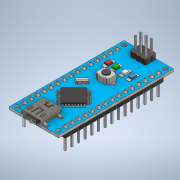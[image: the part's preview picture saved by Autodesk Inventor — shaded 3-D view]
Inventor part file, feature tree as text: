
AUTODESK INVENTOR PART (.ipt)
format: ipt  version: 2021 (Build 250183000, 183)  size: 2,560,000 bytes
history: native  units: mm
features: extrude x33, sketch x32, projected_geometry x27, chamfer x26, fillet x25, mirror x4, plane x3, pattern_circular x1
ambient origin geometry x8: Origin, YZ Plane, XZ Plane, XY Plane, X Axis, Y Axis, Z Axis, Center Point
bodies: Solid1 (feature_tree)
feature tree (151):
  extrude  "Extrusion1"  Depth=18.54199mm
  sketch  "Sketch2"  dims[d2=1.523999mm d3=1.523999mm]
  extrude  "Extrusion2"  Depth=1.523999mm
  extrude  "Extrusion3"  Depth=1.523999mm
  chamfer  "Chamfer1"  Distance=1.0mm
  chamfer  "Chamfer2"  Distance=1.0mm
  chamfer  "Chamfer3"  Distance=0.3mm
  chamfer  "Chamfer4"  Distance=0.7mm Angle=45.0deg
  chamfer  "Chamfer5"  Distance=0.7mm Angle=45.0deg
  chamfer  "Chamfer6"  Distance=0.7mm Angle=45.0deg
  chamfer  "Chamfer7"  Distance=0.7mm Angle=45.0deg
  chamfer  "Chamfer8"  Distance=0.7mm Angle=45.0deg
  chamfer  "Chamfer9"  Distance=0.7mm Angle=45.0deg
  chamfer  "Chamfer10"  Distance=0.7mm Angle=45.0deg
  chamfer  "Chamfer11"  Distance=0.7mm Angle=45.0deg
  chamfer  "Chamfer12"  Distance=0.7mm Angle=45.0deg
  chamfer  "Chamfer13"  Distance=0.7mm Angle=45.0deg
  chamfer  "Chamfer14"  Distance=0.7mm Angle=45.0deg
  chamfer  "Chamfer15"  Distance=0.7mm Angle=45.0deg
  fillet  "Fillet1"  Radius=0.2mm
  sketch  "Sketch6"  dims[d6=1.523999mm]
  plane  "Work Plane1"
  mirror  "Mirror1"
  extrude  "Extrusion5"  Depth=14.0mm TaperAngle=0.0deg
  extrude  "Extrusion6"  Depth=6.0mm TaperAngle=0.0deg
  extrude  "Extrusion7"  Depth=5.0mm
  extrude  "Extrusion8"  Depth=0.3mm
  fillet  "Fillet2"  Radius=0.2mm
  fillet  "Fillet3"  Radius=2.0mm
  fillet  "Fillet4"  Radius=0.5mm
  fillet  "Fillet5"  Radius=0.3mm
  extrude  "Extrusion9"  Depth=0.3mm
  extrude  "Extrusion10"  Depth=1.0mm TaperAngle=0.0deg
  extrude  "Extrusion11"  Depth=0.2mm
  fillet  "Fillet6"  Radius=0.2mm
  fillet  "Fillet7"  Radius=0.1mm
  plane  "Work Plane2"
  mirror  "Mirror2"
  extrude  "Extrusion12"  Depth=1.0mm
  extrude  "Extrusion13"  Depth=8.0mm TaperAngle=0.0deg
  extrude  "Extrusion14"  Depth=0.2mm
  extrude  "Extrusion15"  Depth=0.3mm
  extrude  "Extrusion16"  Depth=0.3mm
  fillet  "Fillet8"  Radius=0.3mm
  fillet  "Fillet9"  Radius=0.5mm
  sketch  "Sketch19"  dims[d115=5.0mm d116=0.0mm d117=0.07mm]
  extrude  "Extrusion17"  Depth=1.0mm TaperAngle=360.0deg
  extrude  "Extrusion18"  Depth=0.2mm
  pattern_circular  "Circular Pattern1"  Angle=45.0deg  [1 undecoded]
  extrude  "Extrusion19"  Depth=0.5mm
  fillet  "Fillet10"  Radius=0.4mm
  fillet  "Fillet11"  Radius=0.5mm
  extrude  "Extrusion20"  Depth=0.4mm
  extrude  "Extrusion21"  Depth=0.7mm TaperAngle=0.0deg
  chamfer  "Chamfer16"  Distance=5.0mm
  fillet  "Fillet12"  Radius=3.5mm
  extrude  "Extrusion22"  Depth=0.3mm
  extrude  "Extrusion23"  Depth=2.0mm TaperAngle=0.0deg
  extrude  "Extrusion24"  Depth=2.5mm
  sketch  "Sketch28"  dims[d174=0.5mm d175=0.0mm d176=0.2mm]
  extrude  "Extrusion25"  Depth=0.2mm TaperAngle=0.0deg
  extrude  "Extrusion26"  Depth=0.7mm TaperAngle=0.0deg
  extrude  "Extrusion27"  Depth=0.2mm TaperAngle=0.0deg
  extrude  "Extrusion28"  Depth=0.2mm
  mirror  "Mirror3"
  fillet  "Fillet13"  Radius=4.0mm
  fillet  "Fillet14"  [1 undecoded]
  fillet  "Fillet15"  Radius=1.1mm
  fillet  "Fillet16"  Radius=1.1mm
  extrude  "Extrusion29"  Depth=0.5mm
  fillet  "Fillet17"  Radius=0.2mm
  fillet  "Fillet18"  Radius=0.2mm
  fillet  "Fillet19"  Radius=0.2mm
  fillet  "Fillet20"  Radius=0.4mm
  fillet  "Fillet21"  Radius=0.2mm
  fillet  "Fillet22"  Radius=0.2mm
  fillet  "Fillet23"  Radius=0.2mm
  fillet  "Fillet24"  Radius=0.2mm
  extrude  "Extrusion30"  Depth=0.2mm
  extrude  "Extrusion31"  Depth=0.2mm
  plane  "Work Plane3"
  extrude  "Extrusion32"  Depth=0.2mm
  extrude  "Extrusion33"  Depth=0.2mm
  chamfer  "Chamfer17"  Distance=3.0mm
  chamfer  "Chamfer18"  Distance=1.25mm
  chamfer  "Chamfer19"  Distance=1.25mm
  chamfer  "Chamfer20"  Distance=0.4mm
  mirror  "Mirror4"
  extrude  "Extrusion34"  Depth=0.4mm
  chamfer  "Chamfer21"  Distance=0.4mm
  chamfer  "Chamfer22"  Distance=0.4mm
  chamfer  "Chamfer23"  Distance=0.4mm
  chamfer  "Chamfer24"  Distance=0.4mm
  chamfer  "Chamfer25"  Distance=0.4mm
  chamfer  "Chamfer26"  Distance=0.4mm
  fillet  "Fillet25"  Radius=0.4mm
  sketch  "Sketch38"  dims[d217=5.0mm d218=0.0mm d219=0.2mm d220=0.5725mm d221=45.0deg d222=0.5mm d235=0.4mm d236=0.0mm d237=0.5mm d238=0.0mm d239=0.4mm d240=0.7mm d241=0.0mm d243=5.0mm d244=3.5mm d245=0.3mm d256=2.0mm d257=0.0mm d259=2.5mm d260=0.6mm d261=0.0mm d262=0.7mm d263=0.0mm d266=0.58mm d267=0.0mm d268=8.597851mm d269=4.0mm d270=0.0mm d273=1.1mm d274=1.1mm d275=0.5mm d276=0.2mm d277=0.2mm d278=0.2mm d279=0.4mm d280=0.0mm d281=0.2mm d282=0.2mm d283=0.2mm d284=0.2mm d285=0.2mm d286=0.2mm d287=0.2mm d288=0.2mm d289=3.0mm d290=0.0mm d297=1.25mm d298=1.25mm d311=0.4mm d312=0.4mm d313=0.4mm d314=0.4mm d315=0.4mm d316=0.4mm d317=0.4mm d318=0.4mm d319=0.4mm d320=0.4mm d321=0.4mm d322=0.4mm d323=0.4mm d324=0.4mm d325=0.4mm d326=0.4mm d327=0.4mm d328=0.4mm d330=2.5mm d331=0.4mm d332=0.4mm d333=1.9mm d334=0.0mm d335=0.0mm d336=0.1mm d337=0.0mm d338=5.0mm d339=0.0mm d340=0.2mm d341=0.5725mm d342=45.0deg d343=0.2mm d344=0.5725mm d345=45.0deg d346=0.2mm d347=0.5725mm d348=45.0deg d349=0.2mm d350=0.5725mm d351=45.0deg d358=1.2mm d359=0.0mm d360=0.6mm d361=1.2mm d362=45.0deg d363=0.6mm d364=1.2mm d365=45.0deg d366=0.6mm d367=1.2mm d368=45.0deg d369=0.6mm d370=1.2mm d371=45.0deg d372=0.6mm d373=1.2mm d374=45.0deg d375=0.6mm d376=1.2mm d377=45.0deg d378=0.2mm]
  sketch  "Sketch1"  dims[d0=43.17998mm d1=18.54199mm]
  sketch  "Sketch3"  dims[d4=1.523999mm d5=1.523999mm]
  projected_geometry  "Projected Loop1"
  projected_geometry  "Projected Loop2"
  projected_geometry  "Projected Loop3"
  projected_geometry  "Projected Loop4"
  projected_geometry  "Projected Loop5"
  projected_geometry  "Projected Loop6"
  projected_geometry  "Projected Loop7"
  projected_geometry  "Projected Loop8"
  projected_geometry  "Projected Loop9"
  projected_geometry  "Projected Loop10"
  projected_geometry  "Projected Loop11"
  projected_geometry  "Projected Loop12"
  projected_geometry  "Projected Loop13"
  sketch  "Sketch7"  dims[d7=0.0mm]
  projected_geometry  "Projected Loop25"
  sketch  "Sketch8"  dims[d8=1.523999mm]
  projected_geometry  "Projected Loop26"
  sketch  "Sketch9"  dims[d9=0.0mm]
  projected_geometry  "Projected Loop27"
  sketch  "Sketch10"  dims[d10=1.777999mm]
  projected_geometry  "Projected Loop28"
  sketch  "Sketch11"  dims[d11=1.777999mm]
  projected_geometry  "Projected Loop29"
  sketch  "Sketch12"  dims[d12=1.777999mm]
  projected_geometry  "Projected Loop30"
  sketch  "Sketch13"  dims[d13=1.777999mm d14=1.0mm d15=0.0mm d31=1.0mm d32=0.0mm d33=0.3mm d34=0.0mm d37=0.7mm d38=0.5725mm d39=45.0deg d40=0.7mm d41=0.5725mm d42=45.0deg d43=0.7mm d44=0.5725mm d45=45.0deg d46=0.7mm d47=0.5725mm d48=45.0deg d49=0.7mm d50=0.5725mm d51=45.0deg d52=0.7mm d53=0.5725mm d54=45.0deg d55=0.7mm d56=0.5725mm d57=45.0deg d58=0.7mm d59=0.5725mm d60=45.0deg d61=0.7mm d62=0.5725mm d63=45.0deg d64=0.7mm d65=0.5725mm d66=45.0deg d67=0.7mm d68=0.5725mm d69=45.0deg d70=0.7mm d71=0.5725mm d72=45.0deg]
  projected_geometry  "Projected Loop31"
  sketch  "Sketch14"  dims[d73=0.7mm d74=0.5725mm d75=45.0deg]
  projected_geometry  "Projected Loop32"
  sketch  "Sketch15"  dims[d76=0.7mm d77=0.5725mm d78=45.0deg]
  sketch  "Sketch16"  dims[d79=0.7mm d80=0.5725mm d81=45.0deg d82=0.2mm]
  sketch  "Sketch17"  dims[d83=-9.271mm d95=14.0mm d96=0.0mm]
  projected_geometry  "Projected Loop33"
  sketch  "Sketch18"  dims[d97=6.0mm d98=0.0mm d105=7.8mm d106=0.0mm]
  projected_geometry  "Projected Loop34"
  projected_geometry  "Projected Loop35"
  sketch  "Sketch20"  dims[d118=0.07mm d119=0.07mm d120=0.2mm d122=2.0mm d131=0.5mm d132=0.0mm d133=0.3mm]
  sketch  "Sketch21"  dims[d134=1.0mm d135=0.3mm]
  sketch  "Sketch22"  dims[d136=1.0mm d137=0.8mm d138=0.0mm]
  projected_geometry  "Projected Loop36"
  sketch  "Sketch24"  dims[d139=7.0mm d140=0.0mm d141=0.2mm d142=0.2mm d143=0.1mm d144=0.0mm]
  sketch  "Sketch25"  dims[d150=1.0mm d151=0.0mm d152=1.1mm]
  projected_geometry  "Projected Loop37"
  sketch  "Sketch26"  dims[d153=0.5mm d154=0.0mm d156=8.0mm d157=0.0mm]
  projected_geometry  "Projected Loop38"
  sketch  "Sketch30"  dims[d177=0.2mm d182=0.3mm]
  sketch  "Sketch31"  dims[d183=0.3mm d184=0.3mm d185=0.3mm d186=0.5mm d187=0.0mm]
  sketch  "Sketch32"  dims[d188=1.0mm d189=0.0mm d190=40.0mm d191=360.0deg]
  sketch  "Sketch33"  dims[d193=0.5mm d194=0.0mm d195=0.2mm]
  sketch  "Sketch34"  dims[d196=0.1mm]
  sketch  "Sketch35"  dims[d210=2.0mm]
  sketch  "Sketch36"  dims[d211=1.9mm d212=0.0mm]
note: 2 required parameter values undecoded (feature->parameter linkage not recoverable at this tier; creation-order binding heuristic only, values carry confidence <= 0.55)
